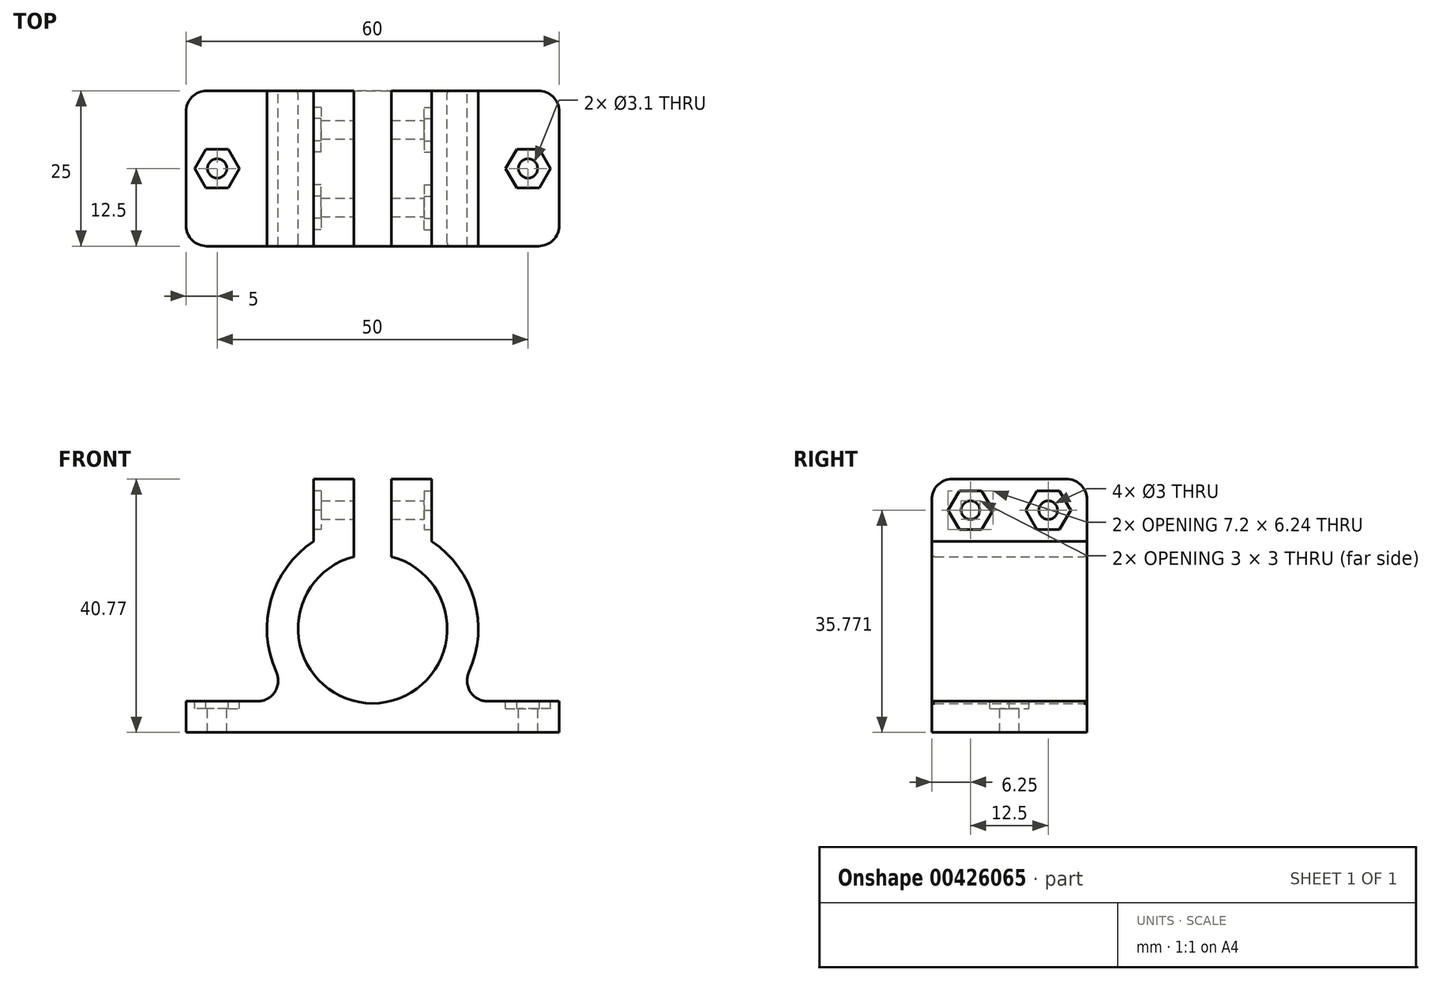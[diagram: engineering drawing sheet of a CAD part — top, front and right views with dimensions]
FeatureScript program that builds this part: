
annotation { "Feature Type Name" : "Feature", "Feature Type Description" : "" }
export const myFeature = defineFeature(function(context is Context, id is Id, definition is map)
    precondition{}
    {
        {
            var Q0;
            Q0=qCreatedBy(makeId("Front.planeOp"),FACE);
            var sketch = newSketch(context, id + "F0", { "sketchPlane" : qUnion([Q0])});
            skLineSegment(sketch, "E0.bottom", {"start": v(30, -27.27) * mm, "end": v(-30, -27.27) * mm});
            skLineSegment(sketch, "E0.left", {"start": v(30, -27.27) * mm, "end": v(30, -22.27) * mm});
            skLineSegment(sketch, "E0.right", {"start": v(-30, -27.27) * mm, "end": v(-30, -22.27) * mm});
            skPoint(sketch, "E0.middle", {"position": v(0, -24.77) * mm});
            skLineSegment(sketch, "E1", {"start": v(0, -27.27) * mm, "end": v(0, 6.08) * mm, "construction": true});
            skArc(sketch, "E2", {"start": v(-3, 1.02) * mm, "mid": v(0, -22.6) * mm, "end": v(3, 1.02) * mm});
            skArc(sketch, "E3.0", {"start": v(12.36, -22.27) * mm, "mid": v(16.9, -8.72) * mm, "end": v(9.5, 3.5) * mm});
            skLineSegment(sketch, "E4", {"start": v(-30, -22.27) * mm, "end": v(-12.36, -22.27) * mm});
            skLineSegment(sketch, "E5.MirrorCS", {"start": v(30, -22.27) * mm, "end": v(12.36, -22.27) * mm});
            skLineSegment(sketch, "E6.top", {"start": v(-9.5, 13.5) * mm, "end": v(-3, 13.5) * mm});
            skLineSegment(sketch, "E6.left", {"start": v(-9.5, 3.5) * mm, "end": v(-9.5, 13.5) * mm});
            skLineSegment(sketch, "E6.right", {"start": v(-3, 4.89) * mm, "end": v(-3, 13.5) * mm});
            skLineSegment(sketch, "E7.MirrorCS", {"start": v(3, 4.89) * mm, "end": v(3, 13.5) * mm});
            skLineSegment(sketch, "E8.MirrorCS", {"start": v(9.5, 3.5) * mm, "end": v(9.5, 13.5) * mm});
            skLineSegment(sketch, "E9.MirrorCS", {"start": v(9.5, 13.5) * mm, "end": v(3, 13.5) * mm});
            skArc(sketch, "E10.trimOffspring", {"start": v(-9.5, 3.5) * mm, "mid": v(-16.9, -8.72) * mm, "end": v(-12.36, -22.27) * mm});
            skPoint(sketch, "E11.orphan", {"position": v(-3, 2.25) * mm});
            skPoint(sketch, "E12.orphan", {"position": v(3, 2.25) * mm});
            skPoint(sketch, "E13.MirrorCS.start.orphan", {"position": v(9.5, 3.5) * mm});
            skLineSegment(sketch, "E14.left", {"start": v(-3, 4.89) * mm, "end": v(-3, 1.02) * mm});
            skLineSegment(sketch, "E14.right", {"start": v(3, 6.14) * mm, "end": v(3, 1.02) * mm});
            skSolve(sketch);
        }
        {
            var Q0;
            Q0=makeQuery(id+"F0.imprint","IMPRINT",FACE,{"disambiguationData":[TD([[makeQuery(id+"F0.imprint","IMPRINT",EDGE,{"derivedFrom":sQuery(id+"F0.wireOp",EDGE,"E0.bottom")}),-1.0]])]});
            extrude(context, id + "F1", {"entities" : qUnion([Q0]), "depth" : 25 * mm});
        }
        {
            var Q0;
            Q0=makeQuery(id+"F1.opExtrude","SWEPT_FACE",FACE,{"disambiguationData":[OSD([sQuery(id+"F0.wireOp",EDGE,"E4")])]});
            var sketch = newSketch(context, id + "F2", { "sketchPlane" : qUnion([Q0])});
            skLineSegment(sketch, "E15", {"start": v(-30, -12.5) * mm, "end": v(30, -12.5) * mm, "construction": true});
            skCircle(sketch, "E16", {"center": v(-25, -12.5) * mm, "radius": 1.55 * mm});
            skCircle(sketch, "E17.MirrorC", {"center": v(25, -12.5) * mm, "radius": 1.55 * mm});
            skSolve(sketch);
        }
        {
            var Q0;
            Q0=qSketchRegion(id+"F2",true);
            extrude(context, id + "F3", {"entities" : qUnion([Q0]), "operationType" : NewBodyOperationType.REMOVE, "oppositeDirection" : true, "depth" : 25 * mm});
        }
        {
            var Q0;
            Q0=makeQuery(id+"F1.opExtrude","SWEPT_FACE",FACE,{"disambiguationData":[OSD([sQuery(id+"F0.wireOp",EDGE,"E8.MirrorCS")])]});
            var sketch = newSketch(context, id + "F4", { "sketchPlane" : qUnion([Q0])});
            skLineSegment(sketch, "E18", {"start": v(-25, 8.5) * mm, "end": v(0, 8.5) * mm, "construction": true});
            skLineSegment(sketch, "E19", {"start": v(-12.5, 13.5) * mm, "end": v(-12.5, 3.5) * mm, "construction": true});
            skLineSegment(sketch, "E20", {"start": v(-18.75, 13.5) * mm, "end": v(-18.75, 3.5) * mm, "construction": true});
            skLineSegment(sketch, "E21.MirrorCS", {"start": v(-6.25, 13.5) * mm, "end": v(-6.25, 3.5) * mm, "construction": true});
            skCircle(sketch, "E22", {"center": v(-18.75, 8.5) * mm, "radius": 1.5 * mm});
            skCircle(sketch, "E23", {"center": v(-6.25, 8.5) * mm, "radius": 1.5 * mm});
            skSolve(sketch);
        }
        {
            var Q0;
            Q0=qSketchRegion(id+"F4",true);
            extrude(context, id + "F5", {"entities" : qUnion([Q0]), "operationType" : NewBodyOperationType.REMOVE, "oppositeDirection" : true, "depth" : 25 * mm});
        }
        {
            var Q0;
            Q0=makeQuery(id+"F1.opExtrude","CAP_EDGE",EDGE,{"disambiguationData":[OSD([sQuery(id+"F0.wireOp",EDGE,"E6.top")])],"isStart":false});
            var Q1;
            Q1=makeQuery(id+"F1.opExtrude","CAP_EDGE",EDGE,{"disambiguationData":[OSD([sQuery(id+"F0.wireOp",EDGE,"E9.MirrorCS")])],"isStart":false});
            var Q2;
            Q2=makeQuery(id+"F1.opExtrude","CAP_EDGE",EDGE,{"disambiguationData":[OSD([sQuery(id+"F0.wireOp",EDGE,"E6.top")])],"isStart":true});
            var Q3;
            Q3=makeQuery(id+"F1.opExtrude","CAP_EDGE",EDGE,{"disambiguationData":[OSD([sQuery(id+"F0.wireOp",EDGE,"E9.MirrorCS")])],"isStart":true});
            var Q4;
            Q4=makeQuery(id+"F1.opExtrude","CAP_EDGE",EDGE,{"disambiguationData":[OSD([sQuery(id+"F0.wireOp",EDGE,"E0.left")])],"isStart":false});
            var Q5;
            Q5=makeQuery(id+"F1.opExtrude","CAP_EDGE",EDGE,{"disambiguationData":[OSD([sQuery(id+"F0.wireOp",EDGE,"E0.left")])],"isStart":true});
            var Q6;
            Q6=makeQuery(id+"F1.opExtrude","CAP_EDGE",EDGE,{"disambiguationData":[OSD([sQuery(id+"F0.wireOp",EDGE,"E0.right")])],"isStart":true});
            var Q7;
            Q7=makeQuery(id+"F1.opExtrude","CAP_EDGE",EDGE,{"disambiguationData":[OSD([sQuery(id+"F0.wireOp",EDGE,"E0.right")])],"isStart":false});
            var Q8;
            Q8=makeQuery(id+"F1.opExtrude","SWEPT_EDGE",EDGE,{"disambiguationData":[OSD([sQuery(id+"F0.wireOp",EDGE,"E3.0"),sQuery(id+"F0.wireOp",EDGE,"E5.MirrorCS")])]});
            var Q9;
            Q9=makeQuery(id+"F1.opExtrude","SWEPT_EDGE",EDGE,{"disambiguationData":[OSD([sQuery(id+"F0.wireOp",EDGE,"E4"),sQuery(id+"F0.wireOp",EDGE,"E10.trimOffspring")])]});
            fillet(context, id + "F6", {"entities" : qUnion([Q0, Q1, Q2, Q3, Q4, Q5, Q6, Q7, Q8, Q9]), "radius" : 3.31 * mm, "tangentPropagation" : true, "allowEdgeOverflow" : false});
        }
        {
            var Q0;
            Q0=makeQuery(id+"F1.opExtrude","SWEPT_FACE",FACE,{"disambiguationData":[OSD([sQuery(id+"F0.wireOp",EDGE,"E8.MirrorCS")])]});
            var sketch = newSketch(context, id + "F7", { "sketchPlane" : qUnion([Q0])});
            skLineSegment(sketch, "E24", {"start": v(-12.5, 3.5) * mm, "end": v(-12.5, 13.5) * mm, "construction": true});
            skLineSegment(sketch, "E25", {"start": v(-12.5, 8.5) * mm, "end": v(-25, 8.5) * mm, "construction": true});
            skLineSegment(sketch, "E26", {"start": v(-12.5, 8.5) * mm, "end": v(0, 8.5) * mm, "construction": true});
            skCircle(sketch, "E27.cCircle", {"center": v(-18.75, 8.5) * mm, "radius": 3.12 * mm, "construction": true});
            skLineSegment(sketch, "E27.0", {"start": v(-16.95, 5.38) * mm, "end": v(-20.55, 5.38) * mm});
            skLineSegment(sketch, "E27.1", {"start": v(-20.55, 5.38) * mm, "end": v(-22.35, 8.5) * mm});
            skLineSegment(sketch, "E27.2", {"start": v(-22.35, 8.5) * mm, "end": v(-20.55, 11.62) * mm});
            skLineSegment(sketch, "E27.3", {"start": v(-20.55, 11.62) * mm, "end": v(-16.95, 11.62) * mm});
            skLineSegment(sketch, "E27.4", {"start": v(-16.95, 11.62) * mm, "end": v(-15.15, 8.5) * mm});
            skLineSegment(sketch, "E27.5", {"start": v(-15.15, 8.5) * mm, "end": v(-16.95, 5.38) * mm});
            skPoint(sketch, "E27.0.midPoint", {"position": v(-18.75, 5.38) * mm});
            skLineSegment(sketch, "E28.MirrorCS", {"start": v(-8.05, 11.62) * mm, "end": v(-9.85, 8.5) * mm});
            skLineSegment(sketch, "E29.MirrorCS", {"start": v(-4.45, 11.62) * mm, "end": v(-8.05, 11.62) * mm});
            skLineSegment(sketch, "E30.MirrorCS", {"start": v(-2.65, 8.5) * mm, "end": v(-4.45, 11.62) * mm});
            skLineSegment(sketch, "E31.MirrorCS", {"start": v(-4.45, 5.38) * mm, "end": v(-2.65, 8.5) * mm});
            skLineSegment(sketch, "E32.MirrorCS", {"start": v(-8.05, 5.38) * mm, "end": v(-4.45, 5.38) * mm});
            skLineSegment(sketch, "E33.MirrorCS", {"start": v(-9.85, 8.5) * mm, "end": v(-8.05, 5.38) * mm});
            skSolve(sketch);
        }
        {
            var Q0;
            Q0=makeQuery(id+"F1.opExtrude","SWEPT_FACE",FACE,{"disambiguationData":[OSD([sQuery(id+"F0.wireOp",EDGE,"E6.left")])]});
            var sketch = newSketch(context, id + "F8", { "sketchPlane" : qUnion([Q0])});
            skLineSegment(sketch, "E34", {"start": v(12.5, 13.5) * mm, "end": v(12.5, 3.5) * mm, "construction": true});
            skLineSegment(sketch, "E35", {"start": v(12.5, 8.5) * mm, "end": v(0, 8.5) * mm, "construction": true});
            skLineSegment(sketch, "E36", {"start": v(12.5, 8.5) * mm, "end": v(25, 8.5) * mm, "construction": true});
            skCircle(sketch, "E37.cCircle", {"center": v(6.25, 8.5) * mm, "radius": 3.12 * mm, "construction": true});
            skLineSegment(sketch, "E37.0", {"start": v(8.05, 5.38) * mm, "end": v(4.45, 5.38) * mm});
            skLineSegment(sketch, "E37.1", {"start": v(4.45, 5.38) * mm, "end": v(2.65, 8.5) * mm});
            skLineSegment(sketch, "E37.2", {"start": v(2.65, 8.5) * mm, "end": v(4.45, 11.62) * mm});
            skLineSegment(sketch, "E37.3", {"start": v(4.45, 11.62) * mm, "end": v(8.05, 11.62) * mm});
            skLineSegment(sketch, "E37.4", {"start": v(8.05, 11.62) * mm, "end": v(9.85, 8.5) * mm});
            skLineSegment(sketch, "E37.5", {"start": v(9.85, 8.5) * mm, "end": v(8.05, 5.38) * mm});
            skPoint(sketch, "E37.0.midPoint", {"position": v(6.25, 5.38) * mm});
            skLineSegment(sketch, "E38.MirrorCS", {"start": v(16.95, 11.62) * mm, "end": v(15.15, 8.5) * mm});
            skLineSegment(sketch, "E39.MirrorCS", {"start": v(20.55, 11.62) * mm, "end": v(16.95, 11.62) * mm});
            skLineSegment(sketch, "E40.MirrorCS", {"start": v(22.35, 8.5) * mm, "end": v(20.55, 11.62) * mm});
            skLineSegment(sketch, "E41.MirrorCS", {"start": v(20.55, 5.38) * mm, "end": v(22.35, 8.5) * mm});
            skLineSegment(sketch, "E42.MirrorCS", {"start": v(16.95, 5.38) * mm, "end": v(20.55, 5.38) * mm});
            skLineSegment(sketch, "E43.MirrorCS", {"start": v(15.15, 8.5) * mm, "end": v(16.95, 5.38) * mm});
            skSolve(sketch);
        }
        {
            var Q0;
            Q0=qSketchRegion(id+"F7",true);
            extrude(context, id + "F9", {"entities" : qUnion([Q0]), "operationType" : NewBodyOperationType.REMOVE, "oppositeDirection" : true, "depth" : 1.2 * mm});
        }
        {
            var Q0;
            Q0=makeQuery(id+"F8.imprint","IMPRINT",FACE,{"disambiguationData":[TD([[makeQuery(id+"F8.imprint","IMPRINT",EDGE,{"derivedFrom":sQuery(id+"F8.wireOp",EDGE,"E37.0")}),-1.0]])]});
            var Q1;
            Q1=makeQuery(id+"F8.imprint","IMPRINT",FACE,{"disambiguationData":[TD([[makeQuery(id+"F8.imprint","IMPRINT",EDGE,{"derivedFrom":sQuery(id+"F8.wireOp",EDGE,"E38.MirrorCS")}),1.0]])]});
            extrude(context, id + "F10", {"entities" : qUnion([Q0, Q1]), "operationType" : NewBodyOperationType.REMOVE, "oppositeDirection" : true, "depth" : 1.2 * mm});
        }
        {
            var Q0;
            Q0=makeQuery(id+"F1.opExtrude","SWEPT_FACE",FACE,{"disambiguationData":[OSD([sQuery(id+"F0.wireOp",EDGE,"E5.MirrorCS")])]});
            var sketch = newSketch(context, id + "F11", { "sketchPlane" : qUnion([Q0])});
            skLineSegment(sketch, "E44", {"start": v(30, -12.5) * mm, "end": v(-33.17, -12.5) * mm, "construction": true});
            skCircle(sketch, "E45.cCircle", {"center": v(25, -12.5) * mm, "radius": 3.12 * mm, "construction": true});
            skLineSegment(sketch, "E45.0", {"start": v(23.2, -9.38) * mm, "end": v(26.8, -9.38) * mm});
            skLineSegment(sketch, "E45.1", {"start": v(26.8, -9.38) * mm, "end": v(28.6, -12.5) * mm});
            skLineSegment(sketch, "E45.2", {"start": v(28.6, -12.5) * mm, "end": v(26.8, -15.62) * mm});
            skLineSegment(sketch, "E45.3", {"start": v(26.8, -15.62) * mm, "end": v(23.2, -15.62) * mm});
            skLineSegment(sketch, "E45.4", {"start": v(23.2, -15.62) * mm, "end": v(21.4, -12.5) * mm});
            skLineSegment(sketch, "E45.5", {"start": v(21.4, -12.5) * mm, "end": v(23.2, -9.38) * mm});
            skPoint(sketch, "E45.0.midPoint", {"position": v(25, -9.38) * mm});
            skLineSegment(sketch, "E46", {"start": v(0, -31.39) * mm, "end": v(0, 22.98) * mm, "construction": true});
            skLineSegment(sketch, "E47.MirrorCS", {"start": v(-21.4, -12.5) * mm, "end": v(-23.2, -9.38) * mm});
            skLineSegment(sketch, "E48.MirrorCS", {"start": v(-23.2, -15.62) * mm, "end": v(-21.4, -12.5) * mm});
            skLineSegment(sketch, "E49.MirrorCS", {"start": v(-26.8, -15.62) * mm, "end": v(-23.2, -15.62) * mm});
            skLineSegment(sketch, "E50.MirrorCS", {"start": v(-28.6, -12.5) * mm, "end": v(-26.8, -15.62) * mm});
            skLineSegment(sketch, "E51.MirrorCS", {"start": v(-26.8, -9.38) * mm, "end": v(-28.6, -12.5) * mm});
            skLineSegment(sketch, "E52.MirrorCS", {"start": v(-23.2, -9.38) * mm, "end": v(-26.8, -9.38) * mm});
            skLineSegment(sketch, "E53", {"start": v(-25, -9.38) * mm, "end": v(-25, -15.62) * mm, "construction": true});
            skSolve(sketch);
        }
        {
            var Q0;
            Q0=qSketchRegion(id+"F11",true);
            extrude(context, id + "F12", {"entities" : qUnion([Q0]), "operationType" : NewBodyOperationType.REMOVE, "oppositeDirection" : true, "depth" : 1.2 * mm});
        }
        {
            var Q0;
            Q0=makeQuery(id+"F1.opExtrude","CAP_EDGE",EDGE,{"disambiguationData":[OSD([sQuery(id+"F0.wireOp",EDGE,"E2")])],"isStart":true});
            var Q1;
            Q1=makeQuery(id+"F1.opExtrude","CAP_EDGE",EDGE,{"disambiguationData":[OSD([sQuery(id+"F0.wireOp",EDGE,"E2")])],"isStart":false});
            fillet(context, id + "F13", {"entities" : qUnion([Q0, Q1]), "radius" : .5 * mm, "tangentPropagation" : true, "allowEdgeOverflow" : false});
        }
    });
